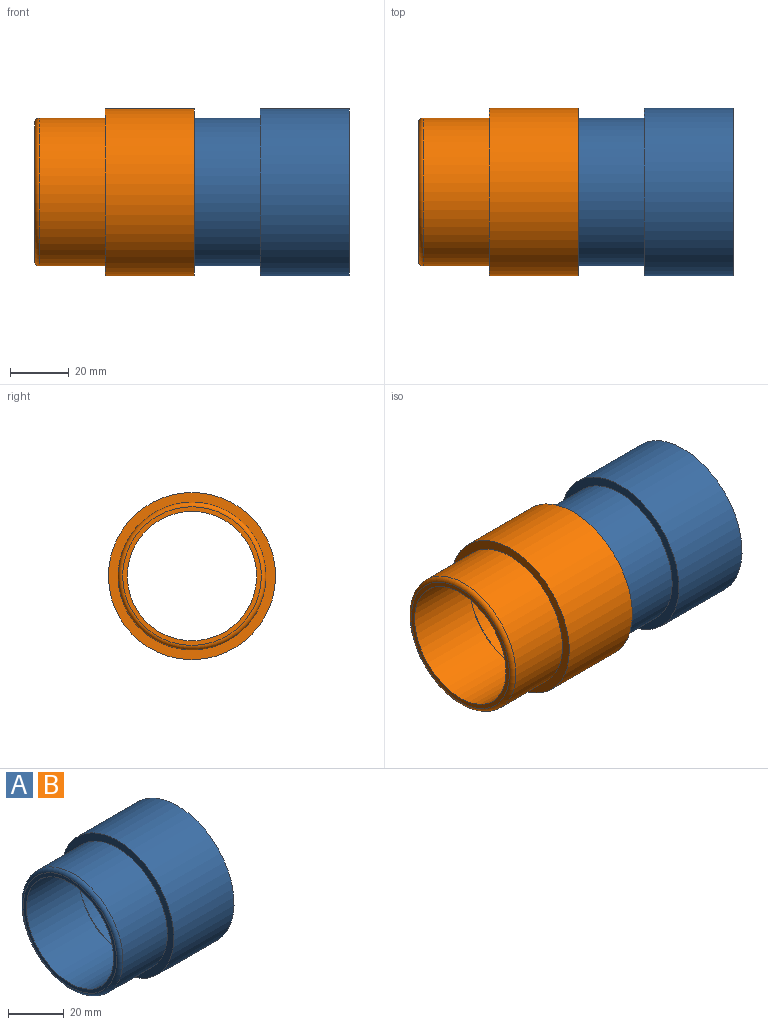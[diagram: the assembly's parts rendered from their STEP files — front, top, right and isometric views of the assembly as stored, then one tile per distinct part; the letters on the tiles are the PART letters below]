
ASSEMBLY  parts=2 mates=1
PART A: 10 faces, bbox 54.6x60.9x60.9 mm
  f0: cylinder r=28.57mm len=57.15mm, axis (-1,0,0), area 5476.6mm2, adj f1,f9
  f1: cone r=25.27mm half-angle=89.6deg, axis (-1,0,0), area 558.6mm2, adj f0,f2
  f2: cylinder r=25.27mm len=50.55mm, axis (-1,0,0), area 3579.6mm2, adj f1,f3
  f3: torus R=23.69mm, axis (-1,0,0), area 386.9mm2, adj f2,f4
  f4: plane 47.37x47.37mm, normal (-1,0,0), area 228.3mm2, adj f3,f5
  f5: cylinder r=22.1mm len=44.2mm, axis (-1,0,0), area 3703mm2, adj f4,f6
  f6: cone r=25.4mm half-angle=52.4deg, axis (1,0,0), area 621.6mm2, adj f5,f7
  f7: cylinder r=25.4mm len=50.8mm, axis (-1,0,0), area 3800.3mm2, adj f6,f8
  f8: torus R=26.99mm, axis (-1,0,0), area 407mm2, adj f7,f9
  f9: plane 57.15x57.15mm, normal (1,0,0), area 277.1mm2, adj f0,f8
PART B: same geometry as A
PLACE A t=(36.32,5.47,-20.75)mm
PLACE B t=(-16.7,5.47,-20.75)mm
MATE slider B.f0 <-> A.f0  axis (1,0,0) through (7.73,5.47,-20.75)mm
